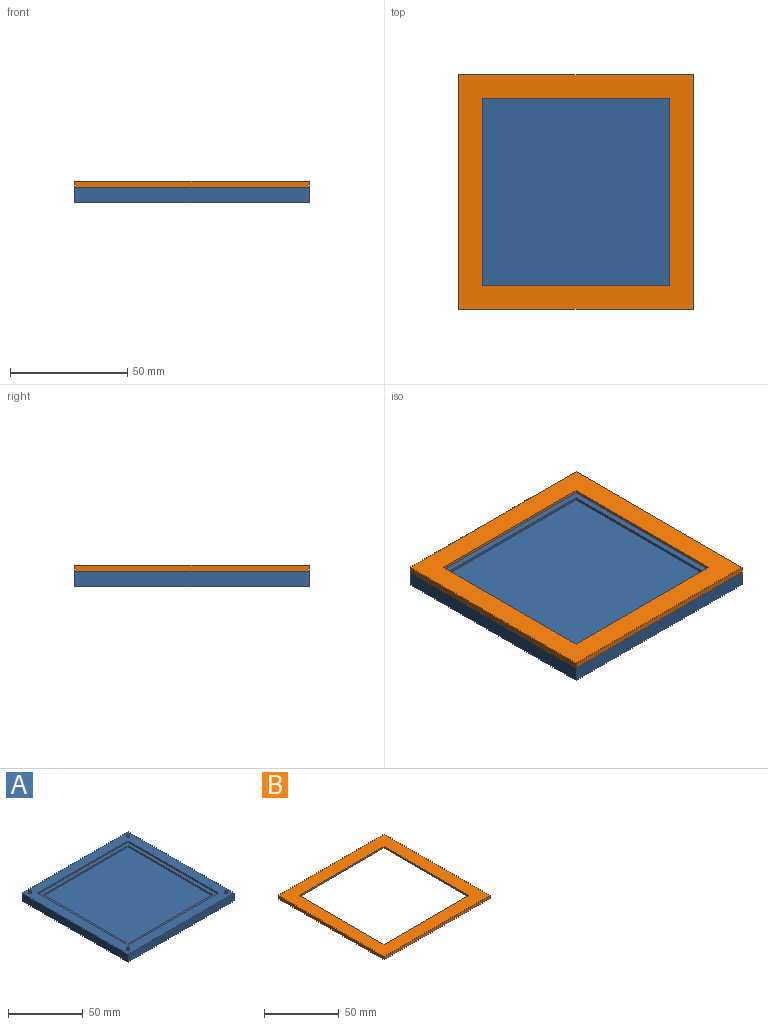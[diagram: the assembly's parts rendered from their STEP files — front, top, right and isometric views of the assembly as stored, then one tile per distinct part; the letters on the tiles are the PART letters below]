
ASSEMBLY  parts=2 mates=1
PART A: 24 faces, bbox 100x100x8 mm
  f0: plane 85x1.25mm, normal (1,0,0), area 106.3mm2, adj f1,f2,f9,f10
  f1: plane 85x1.25mm, normal (0,1,0), area 106.3mm2, adj f0,f3,f9,f10
  f2: plane 85x1.25mm, normal (0,-1,0), area 106.3mm2, adj f0,f3,f9,f10
  f3: plane 85x1.25mm, normal (-1,0,0), area 106.3mm2, adj f1,f2,f9,f10
  f4: plane 80x1.25mm, normal (-1,0,0), area 100mm2, adj f5,f6,f8,f9
  f5: plane 80x1.25mm, normal (0,-1,0), area 100mm2, adj f4,f7,f8,f9
  f6: plane 80x1.25mm, normal (0,1,0), area 100mm2, adj f4,f7,f8,f9
  f7: plane 80x1.25mm, normal (1,0,0), area 100mm2, adj f5,f6,f8,f9
  f8: plane 80x80mm, normal (0,0,1), area 6400mm2, adj f4,f5,f6,f7
  f9: plane 85x85mm, normal (0,0,1), area 825mm2, adj f0,f1,f2,f3,f4,f5,f6,f7
  f10: plane 100x100mm, normal (0,0,1), area 2762.4mm2, adj f0,f1,f2,f3,f12,f13,f14,f15
  f11: plane 100x100mm, normal (0,0,-1), area 10000mm2, adj f12,f13,f14,f15
  f12: plane 100x6.5mm, normal (0,1,0), area 650mm2, adj f10,f11,f13,f15
  f13: plane 100x6.5mm, normal (1,0,0), area 650mm2, adj f10,f11,f12,f14
  f14: plane 100x6.5mm, normal (0,-1,0), area 650mm2, adj f10,f11,f13,f15
  f15: plane 100x6.5mm, normal (-1,0,0), area 650mm2, adj f10,f11,f12,f14
  f16: cylinder r=1mm len=2mm, axis (0,0,-1), area 9.4mm2, adj f10,f17
  f17: plane 2x2mm, normal (0,0,1), area 3.1mm2, adj f16
  f18: cylinder r=1mm len=2mm, axis (0,0,-1), area 9.4mm2, adj f10,f19
  f19: plane 2x2mm, normal (0,0,1), area 3.1mm2, adj f18
  f20: cylinder r=1mm len=2mm, axis (0,0,-1), area 9.4mm2, adj f10,f21
  f21: plane 2x2mm, normal (0,0,1), area 3.1mm2, adj f20
  f22: cylinder r=1mm len=2mm, axis (0,0,-1), area 9.4mm2, adj f10,f23
  f23: plane 2x2mm, normal (0,0,1), area 3.1mm2, adj f22
PART B: 23 faces, bbox 100x100x2.5 mm
  f0: plane 80x1.25mm, normal (0,-1,0), area 100mm2, adj f1,f3,f8,f9
  f1: plane 80x1.25mm, normal (-1,0,0), area 100mm2, adj f0,f2,f3,f9
  f2: plane 80x1.25mm, normal (0,1,0), area 100mm2, adj f1,f3,f8,f9
  f3: plane 100x100mm, normal (0,0,1), area 3600mm2, adj f0,f1,f2,f4,f5,f6,f7,f8
  f4: plane 100x2.5mm, normal (0,1,0), area 250mm2, adj f3,f5,f7,f14
  f5: plane 100x2.5mm, normal (1,0,0), area 250mm2, adj f3,f4,f6,f14
  f6: plane 100x2.5mm, normal (0,-1,0), area 250mm2, adj f3,f5,f7,f14
  f7: plane 100x2.5mm, normal (-1,0,0), area 250mm2, adj f3,f4,f6,f14
  f8: plane 80x1.25mm, normal (1,0,0), area 100mm2, adj f0,f2,f3,f9
  f9: plane 85x85mm, normal (0,0,-1), area 825mm2, adj f0,f1,f2,f8,f10,f11,f12,f13
  f10: plane 85x1.25mm, normal (-1,0,0), area 106.2mm2, adj f9,f11,f12,f14
  f11: plane 85x1.25mm, normal (0,-1,0), area 106.2mm2, adj f9,f10,f13,f14
  f12: plane 85x1.25mm, normal (0,1,0), area 106.2mm2, adj f9,f10,f13,f14
  f13: plane 85x1.25mm, normal (1,0,0), area 106.2mm2, adj f9,f11,f12,f14
  f14: plane 100x100mm, normal (0,0,-1), area 2762.4mm2, adj f4,f5,f6,f7,f10,f11,f12,f13
  f15: cylinder r=1mm len=2mm, axis (0,0,-1), area 9.4mm2, adj f14,f16
  f16: plane 2x2mm, normal (0,0,-1), area 3.1mm2, adj f15
  f17: cylinder r=1mm len=2mm, axis (0,0,-1), area 9.4mm2, adj f14,f18
  f18: plane 2x2mm, normal (0,0,-1), area 3.1mm2, adj f17
  f19: cylinder r=1mm len=2mm, axis (0,0,-1), area 9.4mm2, adj f14,f20
  f20: plane 2x2mm, normal (0,0,-1), area 3.1mm2, adj f19
  f21: cylinder r=1mm len=2mm, axis (0,0,-1), area 9.4mm2, adj f14,f22
  f22: plane 2x2mm, normal (0,0,-1), area 3.1mm2, adj f21
PLACE A t=(-87.39,-72.9,151.78)mm
PLACE B t=(-87.39,-72.9,126.78)mm
MATE slider A.f10 <-> B.f14  axis (0,0,1) through (-87.39,27.1,151.78)mm
